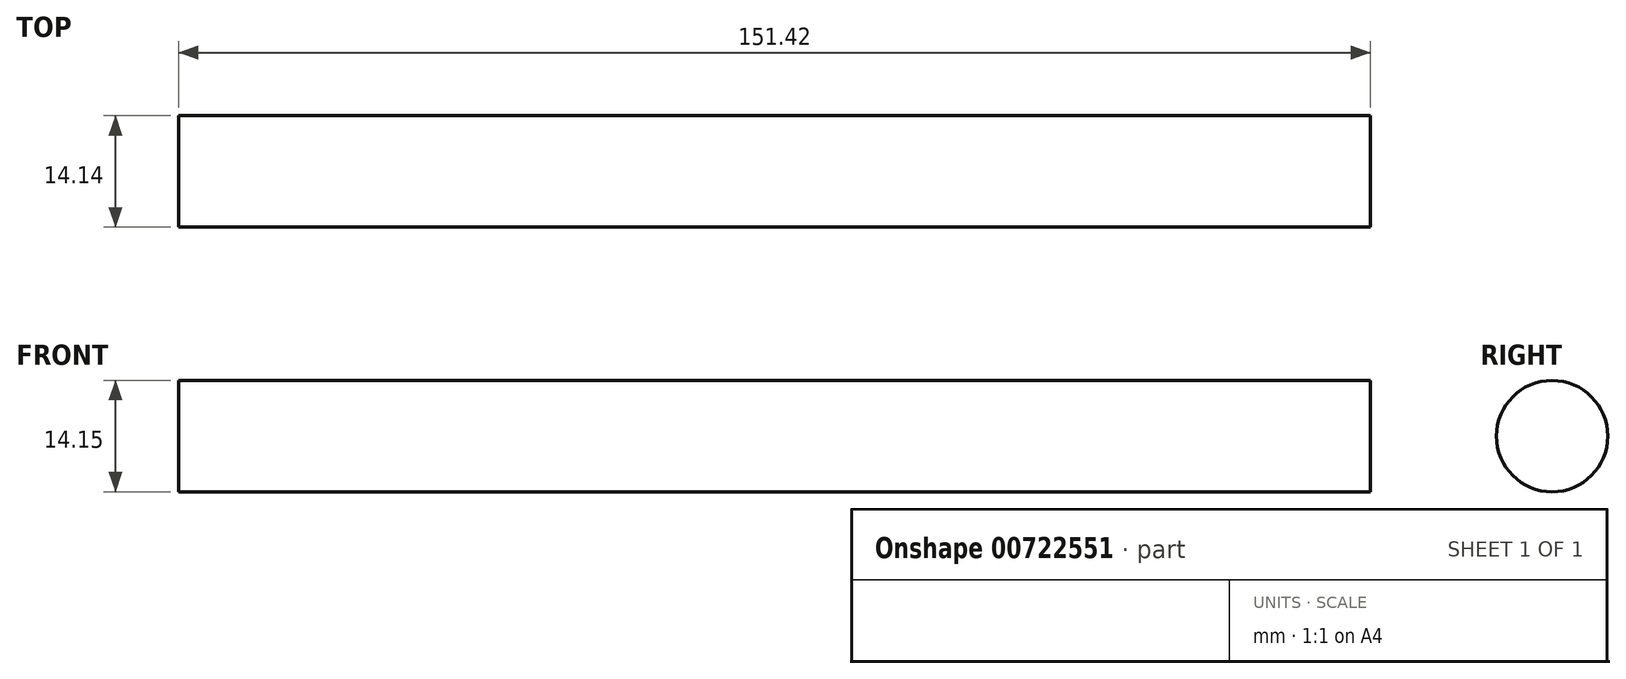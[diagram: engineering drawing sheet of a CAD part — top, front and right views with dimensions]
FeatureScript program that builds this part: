
annotation { "Feature Type Name" : "Feature", "Feature Type Description" : "" }
export const myFeature = defineFeature(function(context is Context, id is Id, definition is map)
    precondition{}
    {
        {
            var Q0;
            Q0=qCreatedBy(makeId("Front.planeOp"),FACE);
            var sketch = newSketch(context, id + "F0", { "sketchPlane" : qUnion([Q0])});
            skLineSegment(sketch, "E0.bottom", {"start": v(-42.53, 25.48) * mm, "end": v(108.89, 25.48) * mm});
            skLineSegment(sketch, "E0.top", {"start": v(-42.53, 32.55) * mm, "end": v(108.89, 32.55) * mm});
            skLineSegment(sketch, "E0.left", {"start": v(-42.53, 25.48) * mm, "end": v(-42.53, 32.55) * mm});
            skLineSegment(sketch, "E0.right", {"start": v(108.89, 25.48) * mm, "end": v(108.89, 32.55) * mm});
            skPoint(sketch, "E1.oppositeSnap0", {"position": v(33.18, 25.48) * mm});
            skLineSegment(sketch, "E1.bottom", {"start": v(33.18, 25.48) * mm, "end": v(33.18, 25.48) * mm});
            skLineSegment(sketch, "E1.top", {"start": v(33.18, 0) * mm, "end": v(33.18, 0) * mm});
            skLineSegment(sketch, "E1.left", {"start": v(33.18, 25.48) * mm, "end": v(33.18, 0) * mm});
            skLineSegment(sketch, "E1.right", {"start": v(33.18, 25.48) * mm, "end": v(33.18, 0) * mm});
            skSolve(sketch);
        }
        {
            var Q0;
            Q0=makeQuery(id+"F0.imprint","IMPRINT",FACE,{"disambiguationData":[TD([[makeQuery(id+"F0.imprint","IMPRINT",EDGE,{"derivedFrom":sQuery(id+"F0.wireOp",EDGE,"E0.top")}),-1.0]])]});
            var Q1;
            Q1=sQuery(id+"F0.wireOp",EDGE,"E0.top");
            revolve(context, id + "F1", {"surfaceOperationType" : NewSurfaceOperationType.NEW, "entities" : qUnion([Q0]), "axis" : qUnion([Q1]), "revolveType" : RevolveType.FULL});
        }
    });
